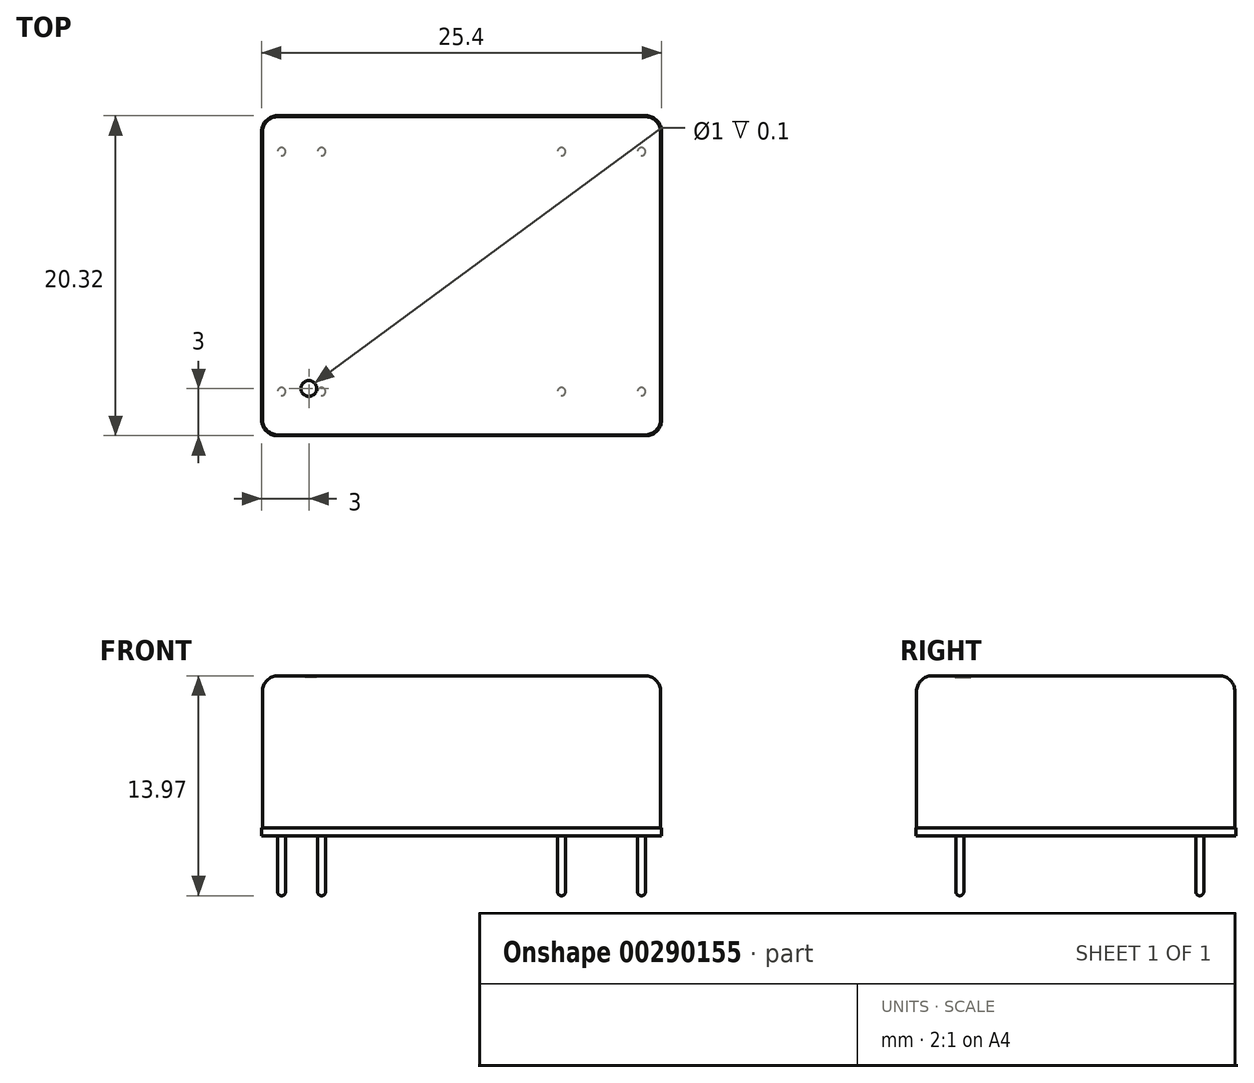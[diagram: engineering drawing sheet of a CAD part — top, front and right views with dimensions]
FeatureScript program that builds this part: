
annotation { "Feature Type Name" : "Feature", "Feature Type Description" : "" }
export const myFeature = defineFeature(function(context is Context, id is Id, definition is map)
    precondition{}
    {
        {
            var Q0;
            Q0=qCreatedBy(makeId("Top.planeOp"),FACE);
            var sketch = newSketch(context, id + "F0", { "sketchPlane" : qUnion([Q0])});
            skLineSegment(sketch, "E0.bottom", {"start": v(0, 0) * mm, "end": v(25.4, 0) * mm});
            skLineSegment(sketch, "E0.top", {"start": v(0, 20.32) * mm, "end": v(25.4, 20.32) * mm});
            skLineSegment(sketch, "E0.left", {"start": v(0, 0) * mm, "end": v(0, 20.32) * mm});
            skLineSegment(sketch, "E0.right", {"start": v(25.4, 0) * mm, "end": v(25.4, 20.32) * mm});
            skSolve(sketch);
        }
        {
            var Q0;
            Q0 = qSketchRegion(id + "F0", true);
            extrude(context, id + "F1", {"entities" : qUnion([Q0]), "depth" : 0.5 * mm});
        }
        {
            var Q0;
            Q0=makeQuery(id+"F1.opExtrude","CAP_FACE",FACE,{"disambiguationData":[OSD([sQuery(id+"F0.wireOp",EDGE,"E0.bottom"),sQuery(id+"F0.wireOp",EDGE,"E0.top"),sQuery(id+"F0.wireOp",EDGE,"E0.left"),sQuery(id+"F0.wireOp",EDGE,"E0.right")])],"isStart":false});
            var sketch = newSketch(context, id + "F2", { "sketchPlane" : qUnion([Q0])});
            skLineSegment(sketch, "E1.0", {"start": v(0.05, 20.27) * mm, "end": v(25.35, 20.27) * mm});
            skLineSegment(sketch, "E1.1", {"start": v(0.05, 0.05) * mm, "end": v(0.05, 20.27) * mm});
            skLineSegment(sketch, "E1.2", {"start": v(0.05, 0.05) * mm, "end": v(25.35, 0.05) * mm});
            skLineSegment(sketch, "E1.3", {"start": v(25.35, 0.05) * mm, "end": v(25.35, 20.27) * mm});
            skSolve(sketch);
        }
        {
            var Q0;
            Q0 = qSketchRegion(id + "F2", true);
            extrude(context, id + "F3", {"entities" : qUnion([Q0]), "operationType" : NewBodyOperationType.ADD, "depth" : 9.65 * mm});
        }
        {
            var Q0;
            Q0=makeQuery(id+"F3.opExtrude","CAP_FACE",FACE,{"disambiguationData":[OSD([sQuery(id+"F2.wireOp",EDGE,"E1.0"),sQuery(id+"F2.wireOp",EDGE,"E1.1"),sQuery(id+"F2.wireOp",EDGE,"E1.2"),sQuery(id+"F2.wireOp",EDGE,"E1.3")])],"isStart":false});
            var sketch = newSketch(context, id + "F4", { "sketchPlane" : qUnion([Q0])});
            skCircle(sketch, "E2", {"center": v(3, 3) * mm, "radius": 0.5 * mm});
            skSolve(sketch);
        }
        {
            var Q0;
            Q0 = qSketchRegion(id + "F4", true);
            extrude(context, id + "F5", {"entities" : qUnion([Q0]), "operationType" : NewBodyOperationType.REMOVE, "oppositeDirection" : true, "depth" : .1 * mm});
        }
        {
            var Q0;
            Q0=makeQuery(id+"F3.opExtrude","SWEPT_EDGE",EDGE,{"disambiguationData":[OSD([sQuery(id+"F2.wireOp",EDGE,"E1.2"),sQuery(id+"F2.wireOp",EDGE,"E1.3")])]});
            var Q1;
            Q1=makeQuery(id+"F3.opExtrude","SWEPT_EDGE",EDGE,{"disambiguationData":[OSD([sQuery(id+"F2.wireOp",EDGE,"E1.0"),sQuery(id+"F2.wireOp",EDGE,"E1.3")])]});
            var Q2;
            Q2=makeQuery(id+"F3.opExtrude","SWEPT_EDGE",EDGE,{"disambiguationData":[OSD([sQuery(id+"F2.wireOp",EDGE,"E1.1"),sQuery(id+"F2.wireOp",EDGE,"E1.2")])]});
            var Q3;
            Q3=makeQuery(id+"F3.opExtrude","SWEPT_EDGE",EDGE,{"disambiguationData":[OSD([sQuery(id+"F2.wireOp",EDGE,"E1.0"),sQuery(id+"F2.wireOp",EDGE,"E1.1")])]});
            var Q4;
            Q4=makeQuery(id+"F1.opExtrude","SWEPT_EDGE",EDGE,{"disambiguationData":[OSD([sQuery(id+"F0.wireOp",EDGE,"E0.bottom"),sQuery(id+"F0.wireOp",EDGE,"E0.right")])]});
            var Q5;
            Q5=makeQuery(id+"F1.opExtrude","SWEPT_EDGE",EDGE,{"disambiguationData":[OSD([sQuery(id+"F0.wireOp",EDGE,"E0.top"),sQuery(id+"F0.wireOp",EDGE,"E0.right")])]});
            var Q6;
            Q6=makeQuery(id+"F1.opExtrude","SWEPT_EDGE",EDGE,{"disambiguationData":[OSD([sQuery(id+"F0.wireOp",EDGE,"E0.bottom"),sQuery(id+"F0.wireOp",EDGE,"E0.left")])]});
            var Q7;
            Q7=makeQuery(id+"F1.opExtrude","SWEPT_EDGE",EDGE,{"disambiguationData":[OSD([sQuery(id+"F0.wireOp",EDGE,"E0.top"),sQuery(id+"F0.wireOp",EDGE,"E0.left")])]});
            var Q8;
            Q8=makeQuery(id+"F3.opExtrude","CAP_EDGE",EDGE,{"disambiguationData":[OSD([sQuery(id+"F2.wireOp",EDGE,"E1.1")])],"isStart":false});
            var Q9;
            Q9=makeQuery(id+"F3.opExtrude","CAP_EDGE",EDGE,{"disambiguationData":[OSD([sQuery(id+"F2.wireOp",EDGE,"E1.0")])],"isStart":false});
            var Q10;
            Q10=makeQuery(id+"F3.opExtrude","CAP_EDGE",EDGE,{"disambiguationData":[OSD([sQuery(id+"F2.wireOp",EDGE,"E1.3")])],"isStart":false});
            var Q11;
            Q11=makeQuery(id+"F3.opExtrude","CAP_EDGE",EDGE,{"disambiguationData":[OSD([sQuery(id+"F2.wireOp",EDGE,"E1.2")])],"isStart":false});
            fillet(context, id + "F6", {"entities" : qUnion([Q0, Q1, Q2, Q3, Q4, Q5, Q6, Q7, Q8, Q9, Q10, Q11]), "radius" : 1 * mm, "tangentPropagation" : true, "allowEdgeOverflow" : false});
        }
        {
            var Q0;
            Q0=qCreatedBy(makeId("Top.planeOp"),FACE);
            var sketch = newSketch(context, id + "F7", { "sketchPlane" : qUnion([Q0])});
            skCircle(sketch, "E3", {"center": v(1.27, 2.8) * mm, "radius": 0.25 * mm});
            skCircle(sketch, "E4", {"center": v(3.81, 2.8) * mm, "radius": 0.25 * mm});
            skCircle(sketch, "E5", {"center": v(1.27, 18.03) * mm, "radius": 0.25 * mm});
            skCircle(sketch, "E6", {"center": v(3.81, 18.03) * mm, "radius": 0.25 * mm});
            skCircle(sketch, "E7", {"center": v(19.05, 18.03) * mm, "radius": 0.25 * mm});
            skCircle(sketch, "E8", {"center": v(24.13, 18.03) * mm, "radius": 0.25 * mm});
            skCircle(sketch, "E9", {"center": v(19.05, 2.8) * mm, "radius": 0.25 * mm});
            skCircle(sketch, "E10", {"center": v(24.13, 2.8) * mm, "radius": 0.25 * mm});
            skLineSegment(sketch, "E11", {"start": v(1.27, 2.8) * mm, "end": v(3.81, 2.8) * mm, "construction": true});
            skLineSegment(sketch, "E12", {"start": v(19.05, 2.8) * mm, "end": v(24.13, 2.8) * mm, "construction": true});
            skLineSegment(sketch, "E13", {"start": v(3.81, 2.8) * mm, "end": v(19.05, 2.8) * mm, "construction": true});
            skLineSegment(sketch, "E14", {"start": v(1.27, 2.8) * mm, "end": v(1.27, 18.03) * mm, "construction": true});
            skLineSegment(sketch, "E15", {"start": v(3.81, 18.03) * mm, "end": v(1.27, 18.03) * mm, "construction": true});
            skLineSegment(sketch, "E16", {"start": v(3.81, 18.03) * mm, "end": v(19.05, 18.03) * mm, "construction": true});
            skLineSegment(sketch, "E17", {"start": v(24.13, 18.03) * mm, "end": v(19.05, 18.03) * mm, "construction": true});
            skSolve(sketch);
        }
        {
            var Q0;
            Q0 = qSketchRegion(id + "F7", true);
            extrude(context, id + "F8", {"entities" : qUnion([Q0]), "operationType" : NewBodyOperationType.ADD, "oppositeDirection" : true, "depth" : 3.8 * mm});
        }
        {
            var Q0;
            Q0=makeQuery(id+"F8.opExtrude","CAP_EDGE",EDGE,{"disambiguationData":[OSD([sQuery(id+"F7.wireOp",EDGE,"E3")])],"isStart":false});
            var Q1;
            Q1=makeQuery(id+"F8.opExtrude","CAP_FACE",FACE,{"disambiguationData":[OSD([sQuery(id+"F7.wireOp",EDGE,"E4")])],"isStart":false});
            var Q2;
            Q2=makeQuery(id+"F8.opExtrude","CAP_FACE",FACE,{"disambiguationData":[OSD([sQuery(id+"F7.wireOp",EDGE,"E10")])],"isStart":false});
            var Q3;
            Q3=makeQuery(id+"F8.opExtrude","CAP_EDGE",EDGE,{"disambiguationData":[OSD([sQuery(id+"F7.wireOp",EDGE,"E9")])],"isStart":false});
            var Q4;
            Q4=makeQuery(id+"F8.opExtrude","CAP_FACE",FACE,{"disambiguationData":[OSD([sQuery(id+"F7.wireOp",EDGE,"E8")])],"isStart":false});
            var Q5;
            Q5=makeQuery(id+"F8.opExtrude","CAP_FACE",FACE,{"disambiguationData":[OSD([sQuery(id+"F7.wireOp",EDGE,"E7")])],"isStart":false});
            var Q6;
            Q6=makeQuery(id+"F8.opExtrude","CAP_EDGE",EDGE,{"disambiguationData":[OSD([sQuery(id+"F7.wireOp",EDGE,"E6")])],"isStart":false});
            var Q7;
            Q7=makeQuery(id+"F8.opExtrude","CAP_FACE",FACE,{"disambiguationData":[OSD([sQuery(id+"F7.wireOp",EDGE,"E5")])],"isStart":false});
            fillet(context, id + "F9", {"entities" : qUnion([Q0, Q1, Q2, Q3, Q4, Q5, Q6, Q7]), "radius" : 0.25 * mm, "tangentPropagation" : true, "allowEdgeOverflow" : false});
        }
    });
